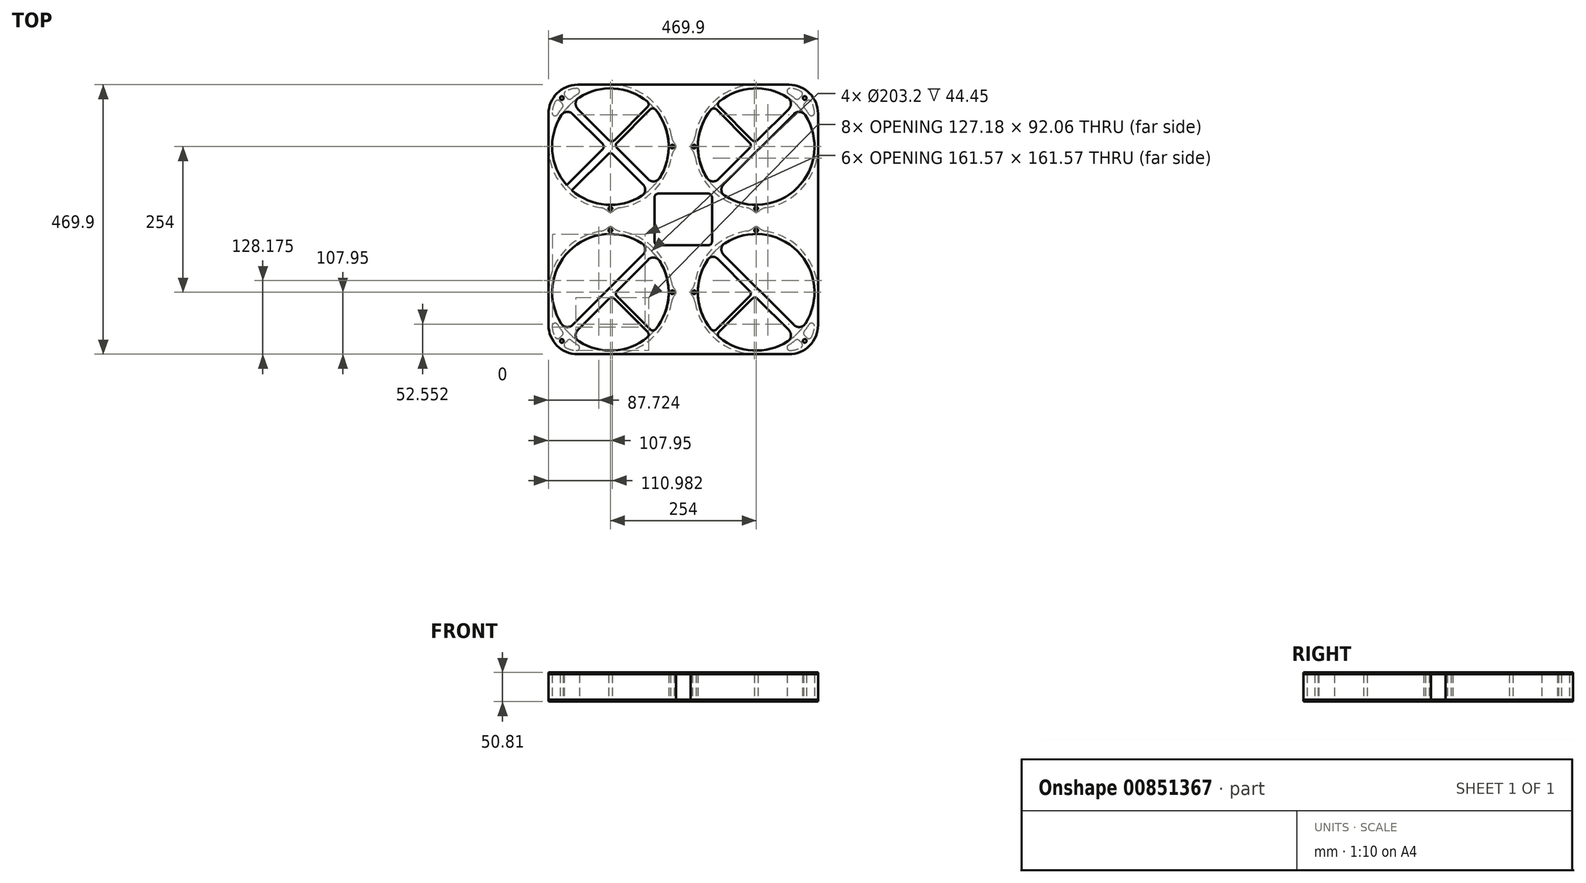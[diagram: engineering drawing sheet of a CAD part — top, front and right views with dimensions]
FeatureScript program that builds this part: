
annotation { "Feature Type Name" : "Feature", "Feature Type Description" : "" }
export const myFeature = defineFeature(function(context is Context, id is Id, definition is map)
    precondition{}
    {
        {
            var Q0;
            Q0=qCreatedBy(makeId("Top.planeOp"),FACE);
            var sketch = newSketch(context, id + "F0", { "sketchPlane" : qUnion([Q0])});
            skLineSegment(sketch, "E0.top", {"start": v(0, 107.95) * mm, "end": v(-57.15, 107.95) * mm});
            skLineSegment(sketch, "E0.right", {"start": v(-107.95, 0) * mm, "end": v(-107.95, 57.15) * mm});
            skPoint(sketch, "E0.middle", {"position": v(0, 0) * mm});
            skCircle(sketch, "E1", {"center": v(0, 0) * mm, "radius": 101.6 * mm});
            skArc(sketch, "E2", {"start": v(17.09, -106.59) * mm, "mid": v(76.33, -76.33) * mm, "end": v(106.59, -17.09) * mm});
            skPoint(sketch, "E3.orphan", {"position": v(107.95, 107.95) * mm});
            skPoint(sketch, "E4.orphan", {"position": v(107.95, -107.95) * mm});
            skPoint(sketch, "E5.orphan", {"position": v(-107.95, -107.95) * mm});
            skArc(sketch, "E6", {"start": v(112.7, -4.22) * mm, "mid": v(114.3, 0) * mm, "end": v(112.7, 4.22) * mm});
            skArc(sketch, "E7", {"start": v(-4.22, -112.7) * mm, "mid": v(0, -114.3) * mm, "end": v(4.22, -112.7) * mm});
            skArc(sketch, "E8.trimOffspring", {"start": v(106.59, 17.09) * mm, "mid": v(70.03, 82.15) * mm, "end": v(0, 107.95) * mm});
            skArc(sketch, "E9.trimOffspring", {"start": v(-107.95, 0) * mm, "mid": v(-82.15, -70.03) * mm, "end": v(-17.09, -106.59) * mm});
            skPoint(sketch, "E10.visualSharp", {"position": v(-107.95, 107.95) * mm});
            skArc(sketch, "E10.filletArc", {"start": v(-57.15, 107.95) * mm, "mid": v(-93.07, 93.07) * mm, "end": v(-107.95, 57.15) * mm});
            skPoint(sketch, "E11.visualSharp", {"position": v(107.76, 6.35) * mm});
            skArc(sketch, "E11.filletArc", {"start": v(106.59, 17.09) * mm, "mid": v(108.72, 10.22) * mm, "end": v(112.7, 4.22) * mm});
            skPoint(sketch, "E12.visualSharp", {"position": v(107.76, -6.35) * mm});
            skArc(sketch, "E12.filletArc", {"start": v(112.7, -4.22) * mm, "mid": v(108.72, -10.22) * mm, "end": v(106.59, -17.09) * mm});
            skPoint(sketch, "E13.visualSharp", {"position": v(6.35, -107.76) * mm});
            skArc(sketch, "E13.filletArc", {"start": v(17.09, -106.59) * mm, "mid": v(10.22, -108.72) * mm, "end": v(4.22, -112.7) * mm});
            skCircle(sketch, "E14", {"center": v(107.95, 0) * mm, "radius": 3.18 * mm});
            skCircle(sketch, "E15", {"center": v(0, -107.95) * mm, "radius": 3.18 * mm});
            skPoint(sketch, "E16.visualSharp", {"position": v(-6.35, -107.76) * mm});
            skArc(sketch, "E16.filletArc", {"start": v(-4.22, -112.7) * mm, "mid": v(-10.22, -108.72) * mm, "end": v(-17.09, -106.59) * mm});
            skCircle(sketch, "E17", {"center": v(-84.7, 84.7) * mm, "radius": 3.18 * mm});
            skArc(sketch, "E18.0", {"start": v(-57.15, 101.6) * mm, "mid": v(-71.18, 99.33) * mm, "end": v(-83.77, 92.75) * mm});
            skLineSegment(sketch, "E19.0", {"start": v(-36.48, 101.6) * mm, "end": v(-57.15, 101.6) * mm});
            skLineSegment(sketch, "E20.0", {"start": v(-101.6, 36.48) * mm, "end": v(-101.6, 57.15) * mm});
            skArc(sketch, "E21.trimOffspring", {"start": v(-36.48, 101.6) * mm, "mid": v(-55.1, 92.83) * mm, "end": v(-71.7, 80.7) * mm});
            skLineSegment(sketch, "E22.0", {"start": v(-92.75, 83.77) * mm, "end": v(-80.7, 71.7) * mm});
            skLineSegment(sketch, "E23.trimOffspring", {"start": v(-83.77, 92.75) * mm, "end": v(-71.7, 80.7) * mm});
            skPoint(sketch, "E24.orphan", {"position": v(-93.07, 93.07) * mm});
            skArc(sketch, "E25.trimOffspring", {"start": v(-92.75, 83.77) * mm, "mid": v(-99.33, 71.18) * mm, "end": v(-101.6, 57.15) * mm});
            skArc(sketch, "E26.trimOffspring", {"start": v(-80.7, 71.7) * mm, "mid": v(-92.83, 55.1) * mm, "end": v(-101.6, 36.48) * mm});
            skSolve(sketch);
        }
        {
            var Q0;
            Q0=makeQuery(id+"F0.imprint","IMPRINT",FACE,{"disambiguationData":[TD([[makeQuery(id+"F0.imprint","IMPRINT",EDGE,{"derivedFrom":sQuery(id+"F0.wireOp",EDGE,"E0.top")}),1.0]])]});
            extrude(context, id + "F1", {"entities" : qUnion([Q0]), "depth" : 44.45 * mm, "offsetDistance" : 25.4 * mm});
        }
        {
            var Q0;
            Q0=makeQuery(id+"F1.opExtrude","SWEPT_EDGE",EDGE,{"disambiguationData":[OSD([sQuery(id+"F0.wireOp",EDGE,"E19.0"),sQuery(id+"F0.wireOp",EDGE,"E21.trimOffspring")])]});
            var Q1;
            Q1=makeQuery(id+"F1.opExtrude","SWEPT_EDGE",EDGE,{"disambiguationData":[OSD([sQuery(id+"F0.wireOp",EDGE,"E21.trimOffspring"),sQuery(id+"F0.wireOp",EDGE,"E23.trimOffspring")])]});
            var Q2;
            Q2=makeQuery(id+"F1.opExtrude","SWEPT_EDGE",EDGE,{"disambiguationData":[OSD([sQuery(id+"F0.wireOp",EDGE,"E18.0"),sQuery(id+"F0.wireOp",EDGE,"E23.trimOffspring")])]});
            var Q3;
            Q3=makeQuery(id+"F1.opExtrude","SWEPT_EDGE",EDGE,{"disambiguationData":[OSD([sQuery(id+"F0.wireOp",EDGE,"E22.0"),sQuery(id+"F0.wireOp",EDGE,"E26.trimOffspring")])]});
            var Q4;
            Q4=makeQuery(id+"F1.opExtrude","SWEPT_EDGE",EDGE,{"disambiguationData":[OSD([sQuery(id+"F0.wireOp",EDGE,"E20.0"),sQuery(id+"F0.wireOp",EDGE,"E26.trimOffspring")])]});
            var Q5;
            Q5=makeQuery(id+"F1.opExtrude","SWEPT_EDGE",EDGE,{"disambiguationData":[OSD([sQuery(id+"F0.wireOp",EDGE,"E22.0"),sQuery(id+"F0.wireOp",EDGE,"E25.trimOffspring")])]});
            fillet(context, id + "F2", {"entities" : qUnion([Q0, Q1, Q2, Q3, Q4, Q5]), "radius" : 5.08 * mm, "tangentPropagation" : true, "allowEdgeOverflow" : false});
        }
        {
            var Q0;
            Q0=makeQuery(id+"F1.opExtrude","SWEPT_BODY",BODY,{"disambiguationData":[OSD([sQuery(id+"F0.wireOp",EDGE,"E0.top"),sQuery(id+"F0.wireOp",EDGE,"E0.right"),sQuery(id+"F0.wireOp",EDGE,"E1"),sQuery(id+"F0.wireOp",EDGE,"E6"),sQuery(id+"F0.wireOp",EDGE,"E7"),sQuery(id+"F0.wireOp",EDGE,"E10.filletArc"),sQuery(id+"F0.wireOp",EDGE,"E11.filletArc"),sQuery(id+"F0.wireOp",EDGE,"E12.filletArc"),sQuery(id+"F0.wireOp",EDGE,"E13.filletArc"),sQuery(id+"F0.wireOp",EDGE,"E14"),sQuery(id+"F0.wireOp",EDGE,"E15"),sQuery(id+"F0.wireOp",EDGE,"E16.filletArc"),sQuery(id+"F0.wireOp",EDGE,"E17"),sQuery(id+"F0.wireOp",EDGE,"E18.0"),sQuery(id+"F0.wireOp",EDGE,"E19.0"),sQuery(id+"F0.wireOp",EDGE,"E9.trimOffspring"),sQuery(id+"F0.wireOp",EDGE,"E20.0"),sQuery(id+"F0.wireOp",EDGE,"E21.trimOffspring"),sQuery(id+"F0.wireOp",EDGE,"E22.0"),sQuery(id+"F0.wireOp",EDGE,"E23.trimOffspring"),sQuery(id+"F0.wireOp",EDGE,"E25.trimOffspring"),sQuery(id+"F0.wireOp",EDGE,"E26.trimOffspring"),sQuery(id+"F0.wireOp",EDGE,"E8.trimOffspring"),sQuery(id+"F0.wireOp",EDGE,"E2")])]});
            var Q1;
            Q1=qCreatedBy(makeId("Right.planeOp"),FACE);
            mirror(context, id + "F3", {"entities" : qUnion([Q0]), "mirrorPlane" : qUnion([Q1])});
        }
        {
            var Q0;
            Q0=makeQuery(id+"F3.opPattern","COPY",BODY,{"derivedFrom":makeQuery(id+"F1.opExtrude","SWEPT_BODY",BODY,{"disambiguationData":[OSD([sQuery(id+"F0.wireOp",EDGE,"E0.top"),sQuery(id+"F0.wireOp",EDGE,"E0.right"),sQuery(id+"F0.wireOp",EDGE,"E1"),sQuery(id+"F0.wireOp",EDGE,"E6"),sQuery(id+"F0.wireOp",EDGE,"E7"),sQuery(id+"F0.wireOp",EDGE,"E10.filletArc"),sQuery(id+"F0.wireOp",EDGE,"E11.filletArc"),sQuery(id+"F0.wireOp",EDGE,"E12.filletArc"),sQuery(id+"F0.wireOp",EDGE,"E13.filletArc"),sQuery(id+"F0.wireOp",EDGE,"E14"),sQuery(id+"F0.wireOp",EDGE,"E15"),sQuery(id+"F0.wireOp",EDGE,"E16.filletArc"),sQuery(id+"F0.wireOp",EDGE,"E17"),sQuery(id+"F0.wireOp",EDGE,"E18.0"),sQuery(id+"F0.wireOp",EDGE,"E19.0"),sQuery(id+"F0.wireOp",EDGE,"E9.trimOffspring"),sQuery(id+"F0.wireOp",EDGE,"E20.0"),sQuery(id+"F0.wireOp",EDGE,"E21.trimOffspring"),sQuery(id+"F0.wireOp",EDGE,"E22.0"),sQuery(id+"F0.wireOp",EDGE,"E23.trimOffspring"),sQuery(id+"F0.wireOp",EDGE,"E25.trimOffspring"),sQuery(id+"F0.wireOp",EDGE,"E26.trimOffspring"),sQuery(id+"F0.wireOp",EDGE,"E8.trimOffspring"),sQuery(id+"F0.wireOp",EDGE,"E2")])]}),"instanceName":"1"});
            var Q1;
            Q1=qCreatedBy(makeId("Front.planeOp"),FACE);
            mirror(context, id + "F4", {"entities" : qUnion([Q0]), "mirrorPlane" : qUnion([Q1])});
        }
        {
            var Q0;
            Q0=makeQuery(id+"F4.opPattern","COPY",BODY,{"derivedFrom":makeQuery(id+"F3.opPattern","COPY",BODY,{"derivedFrom":makeQuery(id+"F1.opExtrude","SWEPT_BODY",BODY,{"disambiguationData":[OSD([sQuery(id+"F0.wireOp",EDGE,"E0.top"),sQuery(id+"F0.wireOp",EDGE,"E0.right"),sQuery(id+"F0.wireOp",EDGE,"E1"),sQuery(id+"F0.wireOp",EDGE,"E6"),sQuery(id+"F0.wireOp",EDGE,"E7"),sQuery(id+"F0.wireOp",EDGE,"E10.filletArc"),sQuery(id+"F0.wireOp",EDGE,"E11.filletArc"),sQuery(id+"F0.wireOp",EDGE,"E12.filletArc"),sQuery(id+"F0.wireOp",EDGE,"E13.filletArc"),sQuery(id+"F0.wireOp",EDGE,"E14"),sQuery(id+"F0.wireOp",EDGE,"E15"),sQuery(id+"F0.wireOp",EDGE,"E16.filletArc"),sQuery(id+"F0.wireOp",EDGE,"E17"),sQuery(id+"F0.wireOp",EDGE,"E18.0"),sQuery(id+"F0.wireOp",EDGE,"E19.0"),sQuery(id+"F0.wireOp",EDGE,"E9.trimOffspring"),sQuery(id+"F0.wireOp",EDGE,"E20.0"),sQuery(id+"F0.wireOp",EDGE,"E21.trimOffspring"),sQuery(id+"F0.wireOp",EDGE,"E22.0"),sQuery(id+"F0.wireOp",EDGE,"E23.trimOffspring"),sQuery(id+"F0.wireOp",EDGE,"E25.trimOffspring"),sQuery(id+"F0.wireOp",EDGE,"E26.trimOffspring"),sQuery(id+"F0.wireOp",EDGE,"E8.trimOffspring"),sQuery(id+"F0.wireOp",EDGE,"E2")])]}),"instanceName":"1"}),"instanceName":"1"});
            var Q1;
            Q1=qCreatedBy(makeId("Right.planeOp"),FACE);
            mirror(context, id + "F5", {"entities" : qUnion([Q0]), "mirrorPlane" : qUnion([Q1])});
        }
        {
            var Q0;
            Q0=makeQuery(id+"F5.opPattern","COPY",BODY,{"derivedFrom":makeQuery(id+"F4.opPattern","COPY",BODY,{"derivedFrom":makeQuery(id+"F3.opPattern","COPY",BODY,{"derivedFrom":makeQuery(id+"F1.opExtrude","SWEPT_BODY",BODY,{"disambiguationData":[OSD([sQuery(id+"F0.wireOp",EDGE,"E0.top"),sQuery(id+"F0.wireOp",EDGE,"E0.right"),sQuery(id+"F0.wireOp",EDGE,"E1"),sQuery(id+"F0.wireOp",EDGE,"E6"),sQuery(id+"F0.wireOp",EDGE,"E7"),sQuery(id+"F0.wireOp",EDGE,"E10.filletArc"),sQuery(id+"F0.wireOp",EDGE,"E11.filletArc"),sQuery(id+"F0.wireOp",EDGE,"E12.filletArc"),sQuery(id+"F0.wireOp",EDGE,"E13.filletArc"),sQuery(id+"F0.wireOp",EDGE,"E14"),sQuery(id+"F0.wireOp",EDGE,"E15"),sQuery(id+"F0.wireOp",EDGE,"E16.filletArc"),sQuery(id+"F0.wireOp",EDGE,"E17"),sQuery(id+"F0.wireOp",EDGE,"E18.0"),sQuery(id+"F0.wireOp",EDGE,"E19.0"),sQuery(id+"F0.wireOp",EDGE,"E9.trimOffspring"),sQuery(id+"F0.wireOp",EDGE,"E20.0"),sQuery(id+"F0.wireOp",EDGE,"E21.trimOffspring"),sQuery(id+"F0.wireOp",EDGE,"E22.0"),sQuery(id+"F0.wireOp",EDGE,"E23.trimOffspring"),sQuery(id+"F0.wireOp",EDGE,"E25.trimOffspring"),sQuery(id+"F0.wireOp",EDGE,"E26.trimOffspring"),sQuery(id+"F0.wireOp",EDGE,"E8.trimOffspring"),sQuery(id+"F0.wireOp",EDGE,"E2")])]}),"instanceName":"1"}),"instanceName":"1"}),"instanceName":"1"});
            transform(context, id + "F6", {"entities" : qUnion([Q0]), "transformType" : TransformType.TRANSLATION_3D, "dx" : 0 * mm, "dy" : -254 * mm, "dz" : 0 * mm, "makeCopy" : false});
        }
        {
            var Q0;
            Q0=makeQuery(id+"F3.opPattern","COPY",BODY,{"derivedFrom":makeQuery(id+"F1.opExtrude","SWEPT_BODY",BODY,{"disambiguationData":[OSD([sQuery(id+"F0.wireOp",EDGE,"E0.top"),sQuery(id+"F0.wireOp",EDGE,"E0.right"),sQuery(id+"F0.wireOp",EDGE,"E1"),sQuery(id+"F0.wireOp",EDGE,"E6"),sQuery(id+"F0.wireOp",EDGE,"E7"),sQuery(id+"F0.wireOp",EDGE,"E10.filletArc"),sQuery(id+"F0.wireOp",EDGE,"E11.filletArc"),sQuery(id+"F0.wireOp",EDGE,"E12.filletArc"),sQuery(id+"F0.wireOp",EDGE,"E13.filletArc"),sQuery(id+"F0.wireOp",EDGE,"E14"),sQuery(id+"F0.wireOp",EDGE,"E15"),sQuery(id+"F0.wireOp",EDGE,"E16.filletArc"),sQuery(id+"F0.wireOp",EDGE,"E17"),sQuery(id+"F0.wireOp",EDGE,"E18.0"),sQuery(id+"F0.wireOp",EDGE,"E19.0"),sQuery(id+"F0.wireOp",EDGE,"E9.trimOffspring"),sQuery(id+"F0.wireOp",EDGE,"E20.0"),sQuery(id+"F0.wireOp",EDGE,"E21.trimOffspring"),sQuery(id+"F0.wireOp",EDGE,"E22.0"),sQuery(id+"F0.wireOp",EDGE,"E23.trimOffspring"),sQuery(id+"F0.wireOp",EDGE,"E25.trimOffspring"),sQuery(id+"F0.wireOp",EDGE,"E26.trimOffspring"),sQuery(id+"F0.wireOp",EDGE,"E8.trimOffspring"),sQuery(id+"F0.wireOp",EDGE,"E2")])]}),"instanceName":"1"});
            transform(context, id + "F7", {"entities" : qUnion([Q0]), "transformType" : TransformType.TRANSLATION_3D, "dx" : 254 * mm, "dy" : 0 * mm, "dz" : 0 * mm, "makeCopy" : false});
        }
        {
            var Q0;
            Q0=makeQuery(id+"F4.opPattern","COPY",BODY,{"derivedFrom":makeQuery(id+"F3.opPattern","COPY",BODY,{"derivedFrom":makeQuery(id+"F1.opExtrude","SWEPT_BODY",BODY,{"disambiguationData":[OSD([sQuery(id+"F0.wireOp",EDGE,"E0.top"),sQuery(id+"F0.wireOp",EDGE,"E0.right"),sQuery(id+"F0.wireOp",EDGE,"E1"),sQuery(id+"F0.wireOp",EDGE,"E6"),sQuery(id+"F0.wireOp",EDGE,"E7"),sQuery(id+"F0.wireOp",EDGE,"E10.filletArc"),sQuery(id+"F0.wireOp",EDGE,"E11.filletArc"),sQuery(id+"F0.wireOp",EDGE,"E12.filletArc"),sQuery(id+"F0.wireOp",EDGE,"E13.filletArc"),sQuery(id+"F0.wireOp",EDGE,"E14"),sQuery(id+"F0.wireOp",EDGE,"E15"),sQuery(id+"F0.wireOp",EDGE,"E16.filletArc"),sQuery(id+"F0.wireOp",EDGE,"E17"),sQuery(id+"F0.wireOp",EDGE,"E18.0"),sQuery(id+"F0.wireOp",EDGE,"E19.0"),sQuery(id+"F0.wireOp",EDGE,"E9.trimOffspring"),sQuery(id+"F0.wireOp",EDGE,"E20.0"),sQuery(id+"F0.wireOp",EDGE,"E21.trimOffspring"),sQuery(id+"F0.wireOp",EDGE,"E22.0"),sQuery(id+"F0.wireOp",EDGE,"E23.trimOffspring"),sQuery(id+"F0.wireOp",EDGE,"E25.trimOffspring"),sQuery(id+"F0.wireOp",EDGE,"E26.trimOffspring"),sQuery(id+"F0.wireOp",EDGE,"E8.trimOffspring"),sQuery(id+"F0.wireOp",EDGE,"E2")])]}),"instanceName":"1"}),"instanceName":"1"});
            transform(context, id + "F8", {"entities" : qUnion([Q0]), "transformType" : TransformType.TRANSLATION_3D, "dx" : 254 * mm, "dy" : -254 * mm, "dz" : 0 * mm, "makeCopy" : false});
        }
        {
            var Q0;
            Q0=makeQuery(id+"F1.opExtrude","CAP_FACE",FACE,{"disambiguationData":[OSD([sQuery(id+"F0.wireOp",EDGE,"E0.top"),sQuery(id+"F0.wireOp",EDGE,"E0.right"),sQuery(id+"F0.wireOp",EDGE,"E1"),sQuery(id+"F0.wireOp",EDGE,"E6"),sQuery(id+"F0.wireOp",EDGE,"E7"),sQuery(id+"F0.wireOp",EDGE,"E10.filletArc"),sQuery(id+"F0.wireOp",EDGE,"E11.filletArc"),sQuery(id+"F0.wireOp",EDGE,"E12.filletArc"),sQuery(id+"F0.wireOp",EDGE,"E13.filletArc"),sQuery(id+"F0.wireOp",EDGE,"E14"),sQuery(id+"F0.wireOp",EDGE,"E15"),sQuery(id+"F0.wireOp",EDGE,"E16.filletArc"),sQuery(id+"F0.wireOp",EDGE,"E17"),sQuery(id+"F0.wireOp",EDGE,"E18.0"),sQuery(id+"F0.wireOp",EDGE,"E19.0"),sQuery(id+"F0.wireOp",EDGE,"E9.trimOffspring"),sQuery(id+"F0.wireOp",EDGE,"E20.0"),sQuery(id+"F0.wireOp",EDGE,"E21.trimOffspring"),sQuery(id+"F0.wireOp",EDGE,"E22.0"),sQuery(id+"F0.wireOp",EDGE,"E23.trimOffspring"),sQuery(id+"F0.wireOp",EDGE,"E25.trimOffspring"),sQuery(id+"F0.wireOp",EDGE,"E26.trimOffspring"),sQuery(id+"F0.wireOp",EDGE,"E8.trimOffspring"),sQuery(id+"F0.wireOp",EDGE,"E2")])],"isStart":false});
            var sketch = newSketch(context, id + "F9", { "sketchPlane" : qUnion([Q0])});
            skArc(sketch, "E27.2", {"start": v(-57.15, 107.95) * mm, "mid": v(-93.07, 93.07) * mm, "end": v(-107.95, 57.15) * mm});
            skArc(sketch, "E27.4", {"start": v(-54.78, -339.57) * mm, "mid": v(5.88, -355.43) * mm, "end": v(64.3, -332.67) * mm});
            skArc(sketch, "E27.5", {"start": v(339.57, -308.78) * mm, "mid": v(325.84, -182.16) * mm, "end": v(199.22, -168.43) * mm});
            skArc(sketch, "E27.6", {"start": v(199.22, -85.57) * mm, "mid": v(325.84, -71.84) * mm, "end": v(339.57, 54.78) * mm});
            skLineSegment(sketch, "E27.7", {"start": v(361.95, 0) * mm, "end": v(361.95, 57.15) * mm});
            skArc(sketch, "E27.8", {"start": v(311.15, 107.95) * mm, "mid": v(347.07, 93.07) * mm, "end": v(361.95, 57.15) * mm});
            skLineSegment(sketch, "E27.9", {"start": v(254, 107.95) * mm, "end": v(311.15, 107.95) * mm});
            skCircle(sketch, "E27.10", {"center": v(338.7, 84.7) * mm, "radius": 3.17 * mm});
            skCircle(sketch, "E27.11", {"center": v(-84.7, 84.7) * mm, "radius": 3.17 * mm});
            skLineSegment(sketch, "E27.12", {"start": v(361.95, -254) * mm, "end": v(361.95, -311.15) * mm});
            skArc(sketch, "E27.13", {"start": v(311.15, -361.95) * mm, "mid": v(347.07, -347.07) * mm, "end": v(361.95, -311.15) * mm});
            skLineSegment(sketch, "E27.14", {"start": v(254, -361.95) * mm, "end": v(311.15, -361.95) * mm});
            skCircle(sketch, "E27.15", {"center": v(338.7, -338.7) * mm, "radius": 3.17 * mm});
            skLineSegment(sketch, "E27.16", {"start": v(0, -361.95) * mm, "end": v(-57.15, -361.95) * mm});
            skArc(sketch, "E27.17", {"start": v(-57.15, -361.95) * mm, "mid": v(-93.07, -347.07) * mm, "end": v(-107.95, -311.15) * mm});
            skLineSegment(sketch, "E27.18", {"start": v(-107.95, -254) * mm, "end": v(-107.95, -311.15) * mm});
            skCircle(sketch, "E27.19", {"center": v(-84.7, -338.7) * mm, "radius": 3.17 * mm});
            skLineSegment(sketch, "E28", {"start": v(0, -361.95) * mm, "end": v(254, -361.95) * mm});
            skLineSegment(sketch, "E29", {"start": v(361.95, -254) * mm, "end": v(361.95, 0) * mm});
            skLineSegment(sketch, "E30", {"start": v(254, 107.95) * mm, "end": v(-57.15, 107.95) * mm});
            skLineSegment(sketch, "E31", {"start": v(-107.95, 57.15) * mm, "end": v(-107.95, -254) * mm});
            skArc(sketch, "E32.0", {"start": v(-85.57, 54.78) * mm, "mid": v(-71.84, -71.84) * mm, "end": v(54.78, -85.57) * mm});
            skCircle(sketch, "E33.0", {"center": v(0, -146.05) * mm, "radius": 3.18 * mm});
            skCircle(sketch, "E33.1", {"center": v(107.95, -254) * mm, "radius": 3.17 * mm});
            skCircle(sketch, "E33.2", {"center": v(254, -146.05) * mm, "radius": 3.18 * mm});
            skCircle(sketch, "E33.3", {"center": v(146.05, -254) * mm, "radius": 3.17 * mm});
            skCircle(sketch, "E33.4", {"center": v(146.05, 0) * mm, "radius": 3.17 * mm});
            skCircle(sketch, "E33.5", {"center": v(254, -107.95) * mm, "radius": 3.18 * mm});
            skLineSegment(sketch, "E34", {"start": v(76.33, -76.33) * mm, "end": v(338.7, -338.7) * mm, "construction": true});
            skLineSegment(sketch, "E35", {"start": v(-84.7, -338.7) * mm, "end": v(338.7, 84.7) * mm, "construction": true});
            skLineSegment(sketch, "E36.0", {"start": v(-56.91, 65.9) * mm, "end": v(-2.25, 11.23) * mm});
            skLineSegment(sketch, "E37.0", {"start": v(-65.9, 56.91) * mm, "end": v(-13.47, 4.5) * mm});
            skArc(sketch, "E38.trimOffspring", {"start": v(85.57, -54.78) * mm, "mid": v(101.43, 5.88) * mm, "end": v(78.67, 64.3) * mm});
            skArc(sketch, "E39.filletArc", {"start": v(54.78, -85.57) * mm, "mid": v(60.56, -76.24) * mm, "end": v(56.91, -65.9) * mm});
            skArc(sketch, "E40.filletArc", {"start": v(-65.9, 56.91) * mm, "mid": v(-76.24, 60.56) * mm, "end": v(-85.57, 54.78) * mm});
            skArc(sketch, "E41.filletArc", {"start": v(-54.78, 85.57) * mm, "mid": v(-60.56, 76.24) * mm, "end": v(-56.91, 65.9) * mm});
            skArc(sketch, "E42.filletArc", {"start": v(65.9, -56.91) * mm, "mid": v(76.24, -60.56) * mm, "end": v(85.57, -54.78) * mm});
            skLineSegment(sketch, "E43.0", {"start": v(-65.9, -310.91) * mm, "end": v(56.91, -188.1) * mm});
            skLineSegment(sketch, "E44.0", {"start": v(-56.91, -319.9) * mm, "end": v(-2.25, -265.23) * mm});
            skLineSegment(sketch, "E45.trimOffspring", {"start": v(188.1, -56.91) * mm, "end": v(242.77, -2.25) * mm});
            skLineSegment(sketch, "E46.trimOffspring", {"start": v(197.09, -65.9) * mm, "end": v(319.9, 56.91) * mm});
            skArc(sketch, "E47.trimOffspring", {"start": v(54.78, -168.43) * mm, "mid": v(-71.84, -182.16) * mm, "end": v(-85.57, -308.78) * mm});
            skArc(sketch, "E48.trimOffspring", {"start": v(308.78, 85.57) * mm, "mid": v(248.12, 101.43) * mm, "end": v(189.7, 78.67) * mm});
            skPoint(sketch, "E49.visualSharp", {"position": v(321.21, 76.2) * mm});
            skArc(sketch, "E49.filletArc", {"start": v(310.91, 65.9) * mm, "mid": v(314.56, 76.24) * mm, "end": v(308.78, 85.57) * mm});
            skPoint(sketch, "E50.visualSharp", {"position": v(330.2, 67.21) * mm});
            skArc(sketch, "E50.filletArc", {"start": v(339.57, 54.78) * mm, "mid": v(330.24, 60.56) * mm, "end": v(319.9, 56.91) * mm});
            skPoint(sketch, "E51.visualSharp", {"position": v(177.8, -67.21) * mm});
            skArc(sketch, "E51.filletArc", {"start": v(168.43, -54.78) * mm, "mid": v(177.76, -60.56) * mm, "end": v(188.1, -56.91) * mm});
            skPoint(sketch, "E52.visualSharp", {"position": v(186.79, -76.2) * mm});
            skArc(sketch, "E52.filletArc", {"start": v(197.09, -65.9) * mm, "mid": v(193.44, -76.24) * mm, "end": v(199.22, -85.57) * mm});
            skPoint(sketch, "E53.visualSharp", {"position": v(67.21, -177.8) * mm});
            skArc(sketch, "E53.filletArc", {"start": v(56.91, -188.1) * mm, "mid": v(60.56, -177.76) * mm, "end": v(54.78, -168.43) * mm});
            skPoint(sketch, "E54.visualSharp", {"position": v(76.2, -186.79) * mm});
            skArc(sketch, "E54.filletArc", {"start": v(85.57, -199.22) * mm, "mid": v(76.24, -193.44) * mm, "end": v(65.9, -197.09) * mm});
            skPoint(sketch, "E55.visualSharp", {"position": v(-76.2, -321.21) * mm});
            skArc(sketch, "E55.filletArc", {"start": v(-85.57, -308.78) * mm, "mid": v(-76.24, -314.56) * mm, "end": v(-65.9, -310.91) * mm});
            skPoint(sketch, "E56.visualSharp", {"position": v(-67.21, -330.2) * mm});
            skArc(sketch, "E56.filletArc", {"start": v(-56.91, -319.9) * mm, "mid": v(-60.56, -330.24) * mm, "end": v(-54.78, -339.57) * mm});
            skArc(sketch, "E57.trimOffspring", {"start": v(170.37, -196.31) * mm, "mid": v(152.48, -258.13) * mm, "end": v(175.33, -318.3) * mm});
            skLineSegment(sketch, "E58.trimOffspring", {"start": v(197.09, -188.1) * mm, "end": v(319.9, -310.91) * mm});
            skLineSegment(sketch, "E59.trimOffspring", {"start": v(185.91, -194.9) * mm, "end": v(242.77, -251.75) * mm});
            skPoint(sketch, "E60.visualSharp", {"position": v(186.79, -177.8) * mm});
            skArc(sketch, "E60.filletArc", {"start": v(199.22, -168.43) * mm, "mid": v(193.44, -177.76) * mm, "end": v(197.09, -188.1) * mm});
            skPoint(sketch, "E61.visualSharp", {"position": v(177.8, -186.79) * mm});
            skArc(sketch, "E61.filletArc", {"start": v(185.91, -194.9) * mm, "mid": v(177.8, -191.96) * mm, "end": v(170.37, -196.31) * mm});
            skPoint(sketch, "E62.visualSharp", {"position": v(321.21, -330.2) * mm});
            skArc(sketch, "E62.filletArc", {"start": v(308.78, -339.57) * mm, "mid": v(314.56, -330.24) * mm, "end": v(310.91, -319.9) * mm});
            skPoint(sketch, "E63.visualSharp", {"position": v(330.2, -321.21) * mm});
            skArc(sketch, "E63.filletArc", {"start": v(319.9, -310.91) * mm, "mid": v(330.24, -314.56) * mm, "end": v(339.57, -308.78) * mm});
            skLineSegment(sketch, "E64", {"start": v(0, 0) * mm, "end": v(76.33, 76.33) * mm, "construction": true});
            skLineSegment(sketch, "E65", {"start": v(0, -254) * mm, "end": v(71.84, -325.84) * mm, "construction": true});
            skLineSegment(sketch, "E66", {"start": v(254, -254) * mm, "end": v(182.16, -325.84) * mm, "construction": true});
            skLineSegment(sketch, "E67.0.left", {"start": v(11.23, -260.74) * mm, "end": v(69.26, -318.77) * mm});
            skLineSegment(sketch, "E67.0.right", {"start": v(6.74, -265.23) * mm, "end": v(64.77, -323.26) * mm});
            skLineSegment(sketch, "E68.0.left", {"start": v(247.26, -265.23) * mm, "end": v(189.23, -323.26) * mm});
            skLineSegment(sketch, "E68.0.right", {"start": v(242.77, -260.74) * mm, "end": v(184.74, -318.77) * mm});
            skLineSegment(sketch, "E69.0.left", {"start": v(6.74, 11.23) * mm, "end": v(64.77, 69.26) * mm});
            skLineSegment(sketch, "E69.0.right", {"start": v(11.23, 6.74) * mm, "end": v(69.26, 64.77) * mm});
            skArc(sketch, "E70.trimOffspring", {"start": v(64.3, 78.67) * mm, "mid": v(5.88, 101.43) * mm, "end": v(-54.78, 85.57) * mm});
            skLineSegment(sketch, "E71.trimOffspring", {"start": v(11.23, -2.25) * mm, "end": v(65.9, -56.91) * mm});
            skPoint(sketch, "E72.visualSharp", {"position": v(69.56, 74.05) * mm});
            skArc(sketch, "E72.filletArc", {"start": v(64.77, 69.26) * mm, "mid": v(66.62, 74.07) * mm, "end": v(64.3, 78.67) * mm});
            skPoint(sketch, "E73.visualSharp", {"position": v(74.05, 69.56) * mm});
            skArc(sketch, "E73.filletArc", {"start": v(78.67, 64.3) * mm, "mid": v(74.07, 66.62) * mm, "end": v(69.26, 64.77) * mm});
            skPoint(sketch, "E74.visualSharp", {"position": v(2.25, 6.74) * mm});
            skArc(sketch, "E74.filletArc", {"start": v(-2.25, 11.23) * mm, "mid": v(2.25, 9.37) * mm, "end": v(6.74, 11.23) * mm});
            skPoint(sketch, "E75.visualSharp", {"position": v(6.74, 2.25) * mm});
            skArc(sketch, "E75.filletArc", {"start": v(11.23, 6.74) * mm, "mid": v(9.37, 2.25) * mm, "end": v(11.23, -2.25) * mm});
            skLineSegment(sketch, "E76", {"start": v(254, 0) * mm, "end": v(182.16, 71.84) * mm, "construction": true});
            skLineSegment(sketch, "E77.0.left", {"start": v(242.77, 6.74) * mm, "end": v(184.74, 64.77) * mm});
            skLineSegment(sketch, "E77.0.right", {"start": v(247.26, 11.23) * mm, "end": v(189.23, 69.26) * mm});
            skArc(sketch, "E78.trimOffspring", {"start": v(175.33, 64.3) * mm, "mid": v(152.57, 5.88) * mm, "end": v(168.43, -54.78) * mm});
            skLineSegment(sketch, "E79.trimOffspring", {"start": v(256.25, 11.23) * mm, "end": v(310.91, 65.9) * mm});
            skLineSegment(sketch, "E80.trimOffspring", {"start": v(256.25, -265.23) * mm, "end": v(310.91, -319.9) * mm});
            skArc(sketch, "E81.trimOffspring", {"start": v(189.7, -332.67) * mm, "mid": v(248.12, -355.43) * mm, "end": v(308.78, -339.57) * mm});
            skLineSegment(sketch, "E82.trimOffspring", {"start": v(11.23, -251.75) * mm, "end": v(65.9, -197.09) * mm});
            skArc(sketch, "E83.trimOffspring", {"start": v(78.67, -318.3) * mm, "mid": v(101.43, -259.88) * mm, "end": v(85.57, -199.22) * mm});
            skPoint(sketch, "E84.visualSharp", {"position": v(6.74, -256.25) * mm});
            skArc(sketch, "E84.filletArc", {"start": v(11.23, -251.75) * mm, "mid": v(9.37, -256.25) * mm, "end": v(11.23, -260.74) * mm});
            skPoint(sketch, "E85.visualSharp", {"position": v(2.25, -260.74) * mm});
            skArc(sketch, "E85.filletArc", {"start": v(6.74, -265.23) * mm, "mid": v(2.25, -263.37) * mm, "end": v(-2.25, -265.23) * mm});
            skPoint(sketch, "E86.visualSharp", {"position": v(247.26, -256.25) * mm});
            skArc(sketch, "E86.filletArc", {"start": v(242.77, -260.74) * mm, "mid": v(244.63, -256.25) * mm, "end": v(242.77, -251.75) * mm});
            skPoint(sketch, "E87.visualSharp", {"position": v(251.75, -260.74) * mm});
            skArc(sketch, "E87.filletArc", {"start": v(256.25, -265.23) * mm, "mid": v(251.75, -263.37) * mm, "end": v(247.26, -265.23) * mm});
            skPoint(sketch, "E88.visualSharp", {"position": v(247.26, 2.25) * mm});
            skArc(sketch, "E88.filletArc", {"start": v(242.77, -2.25) * mm, "mid": v(244.63, 2.25) * mm, "end": v(242.77, 6.74) * mm});
            skPoint(sketch, "E89.visualSharp", {"position": v(251.75, 6.74) * mm});
            skArc(sketch, "E89.filletArc", {"start": v(247.26, 11.23) * mm, "mid": v(251.75, 9.37) * mm, "end": v(256.25, 11.23) * mm});
            skPoint(sketch, "E90.visualSharp", {"position": v(184.44, -328.05) * mm});
            skArc(sketch, "E90.filletArc", {"start": v(189.23, -323.26) * mm, "mid": v(187.38, -328.07) * mm, "end": v(189.7, -332.67) * mm});
            skPoint(sketch, "E91.visualSharp", {"position": v(179.95, -323.56) * mm});
            skArc(sketch, "E91.filletArc", {"start": v(175.33, -318.3) * mm, "mid": v(179.93, -320.62) * mm, "end": v(184.74, -318.77) * mm});
            skPoint(sketch, "E92.visualSharp", {"position": v(74.05, -323.56) * mm});
            skArc(sketch, "E92.filletArc", {"start": v(69.26, -318.77) * mm, "mid": v(74.07, -320.62) * mm, "end": v(78.67, -318.3) * mm});
            skPoint(sketch, "E93.visualSharp", {"position": v(69.56, -328.05) * mm});
            skArc(sketch, "E93.filletArc", {"start": v(64.3, -332.67) * mm, "mid": v(66.62, -328.07) * mm, "end": v(64.77, -323.26) * mm});
            skPoint(sketch, "E94.visualSharp", {"position": v(179.95, 69.56) * mm});
            skArc(sketch, "E94.filletArc", {"start": v(184.74, 64.77) * mm, "mid": v(179.93, 66.62) * mm, "end": v(175.33, 64.3) * mm});
            skPoint(sketch, "E95.visualSharp", {"position": v(184.44, 74.05) * mm});
            skArc(sketch, "E95.filletArc", {"start": v(189.7, 78.67) * mm, "mid": v(187.38, 74.07) * mm, "end": v(189.23, 69.26) * mm});
            skLineSegment(sketch, "E96", {"start": v(0, 0) * mm, "end": v(-71.84, -71.84) * mm, "construction": true});
            skLineSegment(sketch, "E97.0", {"start": v(-13.47, -4.5) * mm, "end": v(-76.33, -67.35) * mm});
            skLineSegment(sketch, "E98.0", {"start": v(-4.5, -13.47) * mm, "end": v(-67.35, -76.33) * mm});
            skLineSegment(sketch, "E99.trimOffspring", {"start": v(4.5, -13.47) * mm, "end": v(56.91, -65.9) * mm});
            skPoint(sketch, "E100.visualSharp", {"position": v(-8.98, 0) * mm});
            skArc(sketch, "E100.filletArc", {"start": v(-13.47, -4.5) * mm, "mid": v(-11.61, 0) * mm, "end": v(-13.47, 4.5) * mm});
            skPoint(sketch, "E101.visualSharp", {"position": v(0, -8.98) * mm});
            skArc(sketch, "E101.filletArc", {"start": v(4.5, -13.47) * mm, "mid": v(0, -11.61) * mm, "end": v(-4.5, -13.47) * mm});
            skSolve(sketch);
        }
        {
            var Q0;
            Q0=makeQuery(id+"F9.imprint","IMPRINT",FACE,{"disambiguationData":[TD([[makeQuery(id+"F9.imprint","IMPRINT",EDGE,{"derivedFrom":sQuery(id+"F9.wireOp",EDGE,"E27.4")}),-1.0]])]});
            var Q1;
            {var subQ23=sQuery(id+"F9.wireOp",EDGE,"E27.2");Q1=makeQuery(id+"F9.imprint","IMPRINT",FACE,{"disambiguationData":[TD([[makeQuery(id+"F9.imprint","IMPRINT",EDGE,{"derivedFrom":subQ23}),1.0]])]});}
            var Q2;
            {var subQ3=sQuery(id+"F0.wireOp",EDGE,"E18.0");Q2=makeQuery(id+"F9.imprint","IMPRINT",FACE,{"disambiguationData":[TD([[makeQuery(id+"F9.imprint","IMPRINT",EDGE,{"derivedFrom":makeQuery(id+"F1.opExtrude","CAP_EDGE",EDGE,{"disambiguationData":[OSD([subQ3])],"isStart":false})}),1.0]])]});}
            var Q3;
            {var subQ0=sQuery(id+"F0.wireOp",EDGE,"E22.0");Q3=makeQuery(id+"F9.imprint","IMPRINT",FACE,{"disambiguationData":[TD([[makeQuery(id+"F9.imprint","IMPRINT",EDGE,{"derivedFrom":makeQuery(id+"F1.opExtrude","CAP_EDGE",EDGE,{"disambiguationData":[OSD([subQ0])],"isStart":false})}),-1.0]])]});}
            var Q4;
            Q4=makeQuery(id+"F9.imprint","IMPRINT",FACE,{"disambiguationData":[TD([[makeQuery(id+"F9.imprint","IMPRINT",EDGE,{"derivedFrom":sQuery(id+"F9.wireOp",EDGE,"E36.0")}),-1.0]])]});
            extrude(context, id + "F10", {"entities" : qUnion([Q0, Q1, Q2, Q3, Q4]), "depth" : 3.17 * mm, "offsetDistance" : 25.4 * mm});
        }
        {
            var Q0;
            Q0=makeQuery(id+"F10.opExtrude","SWEPT_BODY",BODY,{"disambiguationData":[OSD([sQuery(id+"F0.wireOp",EDGE,"E14"),sQuery(id+"F0.wireOp",EDGE,"E15"),sQuery(id+"F9.wireOp",EDGE,"E27.2"),sQuery(id+"F9.wireOp",EDGE,"E27.4"),sQuery(id+"F9.wireOp",EDGE,"E27.5"),sQuery(id+"F9.wireOp",EDGE,"E27.6"),sQuery(id+"F9.wireOp",EDGE,"E27.7"),sQuery(id+"F9.wireOp",EDGE,"E27.8"),sQuery(id+"F9.wireOp",EDGE,"E27.9"),sQuery(id+"F9.wireOp",EDGE,"E27.10"),sQuery(id+"F9.wireOp",EDGE,"E27.11"),sQuery(id+"F9.wireOp",EDGE,"E27.12"),sQuery(id+"F9.wireOp",EDGE,"E27.13"),sQuery(id+"F9.wireOp",EDGE,"E27.14"),sQuery(id+"F9.wireOp",EDGE,"E27.15"),sQuery(id+"F9.wireOp",EDGE,"E27.16"),sQuery(id+"F9.wireOp",EDGE,"E27.17"),sQuery(id+"F9.wireOp",EDGE,"E27.18"),sQuery(id+"F9.wireOp",EDGE,"E27.19"),sQuery(id+"F9.wireOp",EDGE,"E28"),sQuery(id+"F9.wireOp",EDGE,"E29"),sQuery(id+"F9.wireOp",EDGE,"E30"),sQuery(id+"F9.wireOp",EDGE,"E31"),sQuery(id+"F9.wireOp",EDGE,"E32.0"),sQuery(id+"F9.wireOp",EDGE,"E33.0"),sQuery(id+"F9.wireOp",EDGE,"E33.1"),sQuery(id+"F9.wireOp",EDGE,"E33.2"),sQuery(id+"F9.wireOp",EDGE,"E33.3"),sQuery(id+"F9.wireOp",EDGE,"E33.4"),sQuery(id+"F9.wireOp",EDGE,"E33.5"),sQuery(id+"F9.wireOp",EDGE,"E36.0"),sQuery(id+"F9.wireOp",EDGE,"E37.0"),sQuery(id+"F9.wireOp",EDGE,"E38.trimOffspring"),sQuery(id+"F9.wireOp",EDGE,"E39.filletArc"),sQuery(id+"F9.wireOp",EDGE,"E40.filletArc"),sQuery(id+"F9.wireOp",EDGE,"E41.filletArc"),sQuery(id+"F9.wireOp",EDGE,"E42.filletArc"),sQuery(id+"F9.wireOp",EDGE,"E43.0"),sQuery(id+"F9.wireOp",EDGE,"E44.0"),sQuery(id+"F9.wireOp",EDGE,"E45.trimOffspring"),sQuery(id+"F9.wireOp",EDGE,"E46.trimOffspring"),sQuery(id+"F9.wireOp",EDGE,"E47.trimOffspring"),sQuery(id+"F9.wireOp",EDGE,"E48.trimOffspring"),sQuery(id+"F9.wireOp",EDGE,"E49.filletArc"),sQuery(id+"F9.wireOp",EDGE,"E50.filletArc"),sQuery(id+"F9.wireOp",EDGE,"E51.filletArc"),sQuery(id+"F9.wireOp",EDGE,"E52.filletArc"),sQuery(id+"F9.wireOp",EDGE,"E53.filletArc"),sQuery(id+"F9.wireOp",EDGE,"E54.filletArc"),sQuery(id+"F9.wireOp",EDGE,"E55.filletArc"),sQuery(id+"F9.wireOp",EDGE,"E56.filletArc"),sQuery(id+"F9.wireOp",EDGE,"E57.trimOffspring"),sQuery(id+"F9.wireOp",EDGE,"E58.trimOffspring"),sQuery(id+"F9.wireOp",EDGE,"E59.trimOffspring"),sQuery(id+"F9.wireOp",EDGE,"E60.filletArc"),sQuery(id+"F9.wireOp",EDGE,"E61.filletArc"),sQuery(id+"F9.wireOp",EDGE,"E62.filletArc"),sQuery(id+"F9.wireOp",EDGE,"E63.filletArc")])]});
            var Q1;
            Q1=qCreatedBy(makeId("Top.planeOp"),FACE);
            mirror(context, id + "F11", {"entities" : qUnion([Q0]), "mirrorPlane" : qUnion([Q1])});
        }
        {
            var Q0;
            Q0=makeQuery(id+"F11.opPattern","COPY",BODY,{"derivedFrom":makeQuery(id+"F10.opExtrude","SWEPT_BODY",BODY,{"disambiguationData":[OSD([sQuery(id+"F0.wireOp",EDGE,"E14"),sQuery(id+"F0.wireOp",EDGE,"E15"),sQuery(id+"F9.wireOp",EDGE,"E27.2"),sQuery(id+"F9.wireOp",EDGE,"E27.4"),sQuery(id+"F9.wireOp",EDGE,"E27.5"),sQuery(id+"F9.wireOp",EDGE,"E27.6"),sQuery(id+"F9.wireOp",EDGE,"E27.7"),sQuery(id+"F9.wireOp",EDGE,"E27.8"),sQuery(id+"F9.wireOp",EDGE,"E27.9"),sQuery(id+"F9.wireOp",EDGE,"E27.10"),sQuery(id+"F9.wireOp",EDGE,"E27.11"),sQuery(id+"F9.wireOp",EDGE,"E27.12"),sQuery(id+"F9.wireOp",EDGE,"E27.13"),sQuery(id+"F9.wireOp",EDGE,"E27.14"),sQuery(id+"F9.wireOp",EDGE,"E27.15"),sQuery(id+"F9.wireOp",EDGE,"E27.16"),sQuery(id+"F9.wireOp",EDGE,"E27.17"),sQuery(id+"F9.wireOp",EDGE,"E27.18"),sQuery(id+"F9.wireOp",EDGE,"E27.19"),sQuery(id+"F9.wireOp",EDGE,"E28"),sQuery(id+"F9.wireOp",EDGE,"E29"),sQuery(id+"F9.wireOp",EDGE,"E30"),sQuery(id+"F9.wireOp",EDGE,"E31"),sQuery(id+"F9.wireOp",EDGE,"E32.0"),sQuery(id+"F9.wireOp",EDGE,"E33.0"),sQuery(id+"F9.wireOp",EDGE,"E33.1"),sQuery(id+"F9.wireOp",EDGE,"E33.2"),sQuery(id+"F9.wireOp",EDGE,"E33.3"),sQuery(id+"F9.wireOp",EDGE,"E33.4"),sQuery(id+"F9.wireOp",EDGE,"E33.5"),sQuery(id+"F9.wireOp",EDGE,"E36.0"),sQuery(id+"F9.wireOp",EDGE,"E37.0"),sQuery(id+"F9.wireOp",EDGE,"E38.trimOffspring"),sQuery(id+"F9.wireOp",EDGE,"E39.filletArc"),sQuery(id+"F9.wireOp",EDGE,"E40.filletArc"),sQuery(id+"F9.wireOp",EDGE,"E41.filletArc"),sQuery(id+"F9.wireOp",EDGE,"E42.filletArc"),sQuery(id+"F9.wireOp",EDGE,"E43.0"),sQuery(id+"F9.wireOp",EDGE,"E44.0"),sQuery(id+"F9.wireOp",EDGE,"E45.trimOffspring"),sQuery(id+"F9.wireOp",EDGE,"E46.trimOffspring"),sQuery(id+"F9.wireOp",EDGE,"E47.trimOffspring"),sQuery(id+"F9.wireOp",EDGE,"E48.trimOffspring"),sQuery(id+"F9.wireOp",EDGE,"E49.filletArc"),sQuery(id+"F9.wireOp",EDGE,"E50.filletArc"),sQuery(id+"F9.wireOp",EDGE,"E51.filletArc"),sQuery(id+"F9.wireOp",EDGE,"E52.filletArc"),sQuery(id+"F9.wireOp",EDGE,"E53.filletArc"),sQuery(id+"F9.wireOp",EDGE,"E54.filletArc"),sQuery(id+"F9.wireOp",EDGE,"E55.filletArc"),sQuery(id+"F9.wireOp",EDGE,"E56.filletArc"),sQuery(id+"F9.wireOp",EDGE,"E57.trimOffspring"),sQuery(id+"F9.wireOp",EDGE,"E58.trimOffspring"),sQuery(id+"F9.wireOp",EDGE,"E59.trimOffspring"),sQuery(id+"F9.wireOp",EDGE,"E60.filletArc"),sQuery(id+"F9.wireOp",EDGE,"E61.filletArc"),sQuery(id+"F9.wireOp",EDGE,"E62.filletArc"),sQuery(id+"F9.wireOp",EDGE,"E63.filletArc")])]}),"instanceName":"1"});
            transform(context, id + "F12", {"entities" : qUnion([Q0]), "transformType" : TransformType.TRANSLATION_3D, "dx" : 0 * mm, "dy" : 0 * mm, "dz" : 44.45 * mm, "makeCopy" : false});
        }
        {
            var Q0;
            Q0=makeQuery(id+"F10.opExtrude","CAP_FACE",FACE,{"disambiguationData":[OSD([sQuery(id+"F0.wireOp",EDGE,"E14"),sQuery(id+"F0.wireOp",EDGE,"E15"),sQuery(id+"F9.wireOp",EDGE,"E27.2"),sQuery(id+"F9.wireOp",EDGE,"E27.4"),sQuery(id+"F9.wireOp",EDGE,"E27.5"),sQuery(id+"F9.wireOp",EDGE,"E27.6"),sQuery(id+"F9.wireOp",EDGE,"E27.7"),sQuery(id+"F9.wireOp",EDGE,"E27.8"),sQuery(id+"F9.wireOp",EDGE,"E27.9"),sQuery(id+"F9.wireOp",EDGE,"E27.10"),sQuery(id+"F9.wireOp",EDGE,"E27.11"),sQuery(id+"F9.wireOp",EDGE,"E27.12"),sQuery(id+"F9.wireOp",EDGE,"E27.13"),sQuery(id+"F9.wireOp",EDGE,"E27.14"),sQuery(id+"F9.wireOp",EDGE,"E27.15"),sQuery(id+"F9.wireOp",EDGE,"E27.16"),sQuery(id+"F9.wireOp",EDGE,"E27.17"),sQuery(id+"F9.wireOp",EDGE,"E27.18"),sQuery(id+"F9.wireOp",EDGE,"E27.19"),sQuery(id+"F9.wireOp",EDGE,"E28"),sQuery(id+"F9.wireOp",EDGE,"E29"),sQuery(id+"F9.wireOp",EDGE,"E30"),sQuery(id+"F9.wireOp",EDGE,"E31"),sQuery(id+"F9.wireOp",EDGE,"E32.0"),sQuery(id+"F9.wireOp",EDGE,"E33.0"),sQuery(id+"F9.wireOp",EDGE,"E33.1"),sQuery(id+"F9.wireOp",EDGE,"E33.2"),sQuery(id+"F9.wireOp",EDGE,"E33.3"),sQuery(id+"F9.wireOp",EDGE,"E33.4"),sQuery(id+"F9.wireOp",EDGE,"E33.5"),sQuery(id+"F9.wireOp",EDGE,"E36.0"),sQuery(id+"F9.wireOp",EDGE,"E37.0"),sQuery(id+"F9.wireOp",EDGE,"E38.trimOffspring"),sQuery(id+"F9.wireOp",EDGE,"E39.filletArc"),sQuery(id+"F9.wireOp",EDGE,"E40.filletArc"),sQuery(id+"F9.wireOp",EDGE,"E41.filletArc"),sQuery(id+"F9.wireOp",EDGE,"E42.filletArc"),sQuery(id+"F9.wireOp",EDGE,"E43.0"),sQuery(id+"F9.wireOp",EDGE,"E44.0"),sQuery(id+"F9.wireOp",EDGE,"E45.trimOffspring"),sQuery(id+"F9.wireOp",EDGE,"E46.trimOffspring"),sQuery(id+"F9.wireOp",EDGE,"E47.trimOffspring"),sQuery(id+"F9.wireOp",EDGE,"E48.trimOffspring"),sQuery(id+"F9.wireOp",EDGE,"E49.filletArc"),sQuery(id+"F9.wireOp",EDGE,"E50.filletArc"),sQuery(id+"F9.wireOp",EDGE,"E51.filletArc"),sQuery(id+"F9.wireOp",EDGE,"E52.filletArc"),sQuery(id+"F9.wireOp",EDGE,"E53.filletArc"),sQuery(id+"F9.wireOp",EDGE,"E54.filletArc"),sQuery(id+"F9.wireOp",EDGE,"E55.filletArc"),sQuery(id+"F9.wireOp",EDGE,"E56.filletArc"),sQuery(id+"F9.wireOp",EDGE,"E57.trimOffspring"),sQuery(id+"F9.wireOp",EDGE,"E58.trimOffspring"),sQuery(id+"F9.wireOp",EDGE,"E59.trimOffspring"),sQuery(id+"F9.wireOp",EDGE,"E60.filletArc"),sQuery(id+"F9.wireOp",EDGE,"E61.filletArc"),sQuery(id+"F9.wireOp",EDGE,"E62.filletArc"),sQuery(id+"F9.wireOp",EDGE,"E63.filletArc"),sQuery(id+"F9.wireOp",EDGE,"E67.0.left"),sQuery(id+"F9.wireOp",EDGE,"E67.0.right"),sQuery(id+"F9.wireOp",EDGE,"E68.0.left"),sQuery(id+"F9.wireOp",EDGE,"E68.0.right"),sQuery(id+"F9.wireOp",EDGE,"E69.0.left"),sQuery(id+"F9.wireOp",EDGE,"E69.0.right"),sQuery(id+"F9.wireOp",EDGE,"E70.trimOffspring"),sQuery(id+"F9.wireOp",EDGE,"E71.trimOffspring"),sQuery(id+"F9.wireOp",EDGE,"E72.filletArc"),sQuery(id+"F9.wireOp",EDGE,"E73.filletArc"),sQuery(id+"F9.wireOp",EDGE,"E74.filletArc"),sQuery(id+"F9.wireOp",EDGE,"E75.filletArc"),sQuery(id+"F9.wireOp",EDGE,"E77.0.left"),sQuery(id+"F9.wireOp",EDGE,"E77.0.right"),sQuery(id+"F9.wireOp",EDGE,"E78.trimOffspring"),sQuery(id+"F9.wireOp",EDGE,"E79.trimOffspring"),sQuery(id+"F9.wireOp",EDGE,"E80.trimOffspring"),sQuery(id+"F9.wireOp",EDGE,"E81.trimOffspring"),sQuery(id+"F9.wireOp",EDGE,"E82.trimOffspring"),sQuery(id+"F9.wireOp",EDGE,"E83.trimOffspring"),sQuery(id+"F9.wireOp",EDGE,"E84.filletArc"),sQuery(id+"F9.wireOp",EDGE,"E85.filletArc"),sQuery(id+"F9.wireOp",EDGE,"E86.filletArc"),sQuery(id+"F9.wireOp",EDGE,"E87.filletArc"),sQuery(id+"F9.wireOp",EDGE,"E88.filletArc"),sQuery(id+"F9.wireOp",EDGE,"E89.filletArc"),sQuery(id+"F9.wireOp",EDGE,"E90.filletArc"),sQuery(id+"F9.wireOp",EDGE,"E91.filletArc"),sQuery(id+"F9.wireOp",EDGE,"E92.filletArc"),sQuery(id+"F9.wireOp",EDGE,"E93.filletArc"),sQuery(id+"F9.wireOp",EDGE,"E94.filletArc"),sQuery(id+"F9.wireOp",EDGE,"E95.filletArc")])],"isStart":false});
            var sketch = newSketch(context, id + "F13", { "sketchPlane" : qUnion([Q0])});
            skLineSegment(sketch, "E102", {"start": v(-107.95, -127) * mm, "end": v(361.95, -127) * mm, "construction": true});
            skLineSegment(sketch, "E103", {"start": v(127, 107.95) * mm, "end": v(127, -361.95) * mm, "construction": true});
            skLineSegment(sketch, "E104.bottom", {"start": v(170.65, -172) * mm, "end": v(83.35, -172) * mm});
            skLineSegment(sketch, "E104.top", {"start": v(170.65, -82) * mm, "end": v(83.35, -82) * mm});
            skLineSegment(sketch, "E104.left", {"start": v(177, -165.65) * mm, "end": v(177, -88.35) * mm});
            skLineSegment(sketch, "E104.right", {"start": v(77, -165.65) * mm, "end": v(77, -88.35) * mm});
            skPoint(sketch, "E104.middle", {"position": v(127, -127) * mm});
            skPoint(sketch, "E105.visualSharp", {"position": v(77, -82) * mm});
            skArc(sketch, "E105.filletArc", {"start": v(83.35, -82) * mm, "mid": v(78.86, -83.86) * mm, "end": v(77, -88.35) * mm});
            skPoint(sketch, "E106.visualSharp", {"position": v(77, -172) * mm});
            skArc(sketch, "E106.filletArc", {"start": v(77, -165.65) * mm, "mid": v(78.86, -170.14) * mm, "end": v(83.35, -172) * mm});
            skPoint(sketch, "E107.visualSharp", {"position": v(177, -82) * mm});
            skArc(sketch, "E107.filletArc", {"start": v(177, -88.35) * mm, "mid": v(175.14, -83.86) * mm, "end": v(170.65, -82) * mm});
            skPoint(sketch, "E108.visualSharp", {"position": v(177, -172) * mm});
            skArc(sketch, "E108.filletArc", {"start": v(170.65, -172) * mm, "mid": v(175.14, -170.14) * mm, "end": v(177, -165.65) * mm});
            skSolve(sketch);
        }
        {
            var Q0;
            Q0=makeQuery(id+"F13.imprint","IMPRINT",FACE,{"disambiguationData":[TD([[makeQuery(id+"F13.imprint","IMPRINT",EDGE,{"derivedFrom":sQuery(id+"F13.wireOp",EDGE,"E104.bottom")}),-1.0]])]});
            var Q1;
            Q1 = qSketchRegion(id + "F13", true);
            extrude(context, id + "F14", {"entities" : qUnion([Q0, Q1]), "operationType" : NewBodyOperationType.REMOVE, "oppositeDirection" : true, "depth" : 8.58 * mm, "offsetDistance" : 25.4 * mm});
        }
    });
